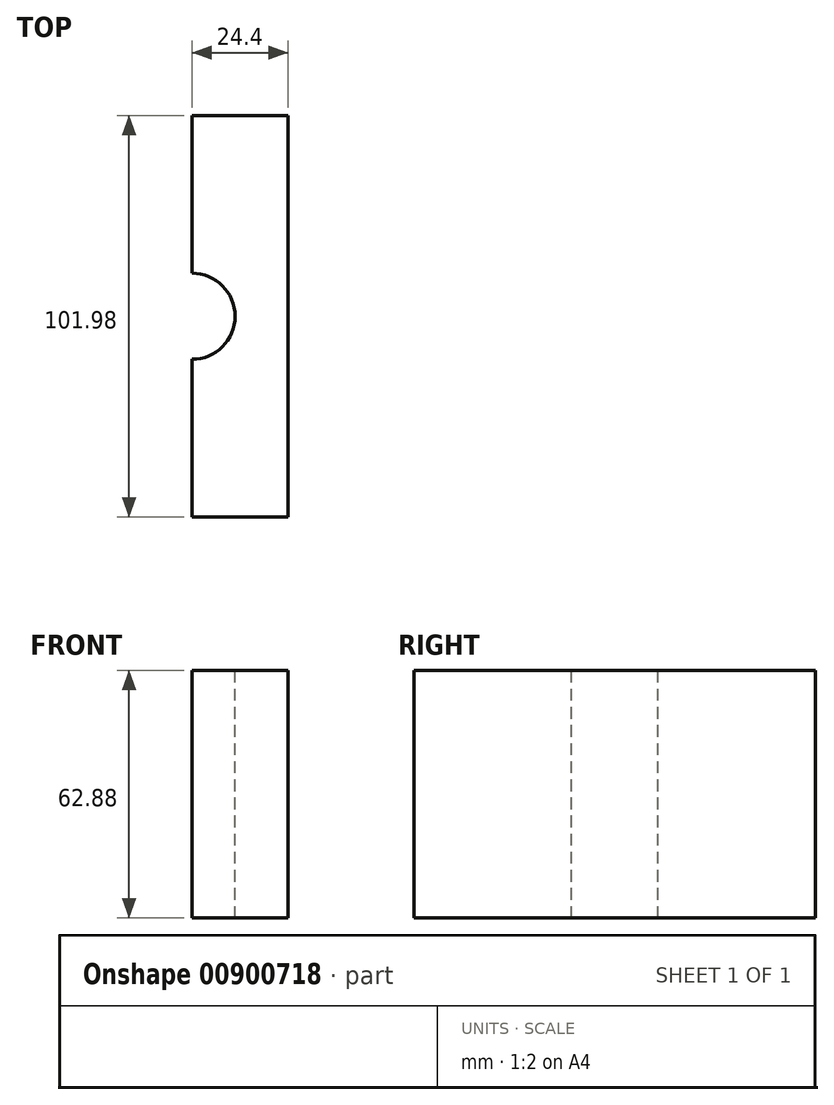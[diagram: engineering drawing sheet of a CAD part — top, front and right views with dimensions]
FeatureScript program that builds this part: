
annotation { "Feature Type Name" : "Feature", "Feature Type Description" : "" }
export const myFeature = defineFeature(function(context is Context, id is Id, definition is map)
    precondition{}
    {
        {
            var Q0;
            Q0=qCreatedBy(makeId("Top.planeOp"),FACE);
            var sketch = newSketch(context, id + "F0", { "sketchPlane" : qUnion([Q0])});
            skLineSegment(sketch, "E0.bottom", {"start": v(12.2, 50.99) * mm, "end": v(-12.2, 50.99) * mm});
            skLineSegment(sketch, "E0.top", {"start": v(12.2, -50.99) * mm, "end": v(-12.2, -50.99) * mm});
            skLineSegment(sketch, "E0.left", {"start": v(12.2, 50.99) * mm, "end": v(12.2, -50.99) * mm});
            skLineSegment(sketch, "E0.right", {"start": v(-12.2, 50.99) * mm, "end": v(-12.2, -50.99) * mm});
            skPoint(sketch, "E0.middle", {"position": v(0, 0) * mm});
            skCircle(sketch, "E1", {"center": v(-12.2, 0) * mm, "radius": 10.93 * mm});
            skSolve(sketch);
        }
        {
            var Q0;
            {var subQ1=sQuery(id+"F0.wireOp",EDGE,"E0.bottom");Q0=makeQuery(id+"F0.imprint","IMPRINT",FACE,{"disambiguationData":[TD([[makeQuery(id+"F0.imprint","IMPRINT",EDGE,{"derivedFrom":subQ1}),1.0]])]});}
            extrude(context, id + "F1", {"entities" : qUnion([Q0]), "oppositeDirection" : true, "depth" : 32.32 * mm, "offsetDistance" : 25.4 * mm});
        }
        {
            var Q0;
            Q0=makeQuery(id+"F1.opExtrude","CAP_FACE",FACE,{"disambiguationData":[OSD([sQuery(id+"F0.wireOp",EDGE,"E0.bottom"),sQuery(id+"F0.wireOp",EDGE,"E0.top"),sQuery(id+"F0.wireOp",EDGE,"E0.left"),sQuery(id+"F0.wireOp",EDGE,"E0.right"),sQuery(id+"F0.wireOp",EDGE,"E1")])],"isStart":true});
            extrude(context, id + "F2", {"entities" : qUnion([Q0]), "operationType" : NewBodyOperationType.ADD, "depth" : 30.56 * mm, "offsetDistance" : 25.4 * mm});
        }
    });
